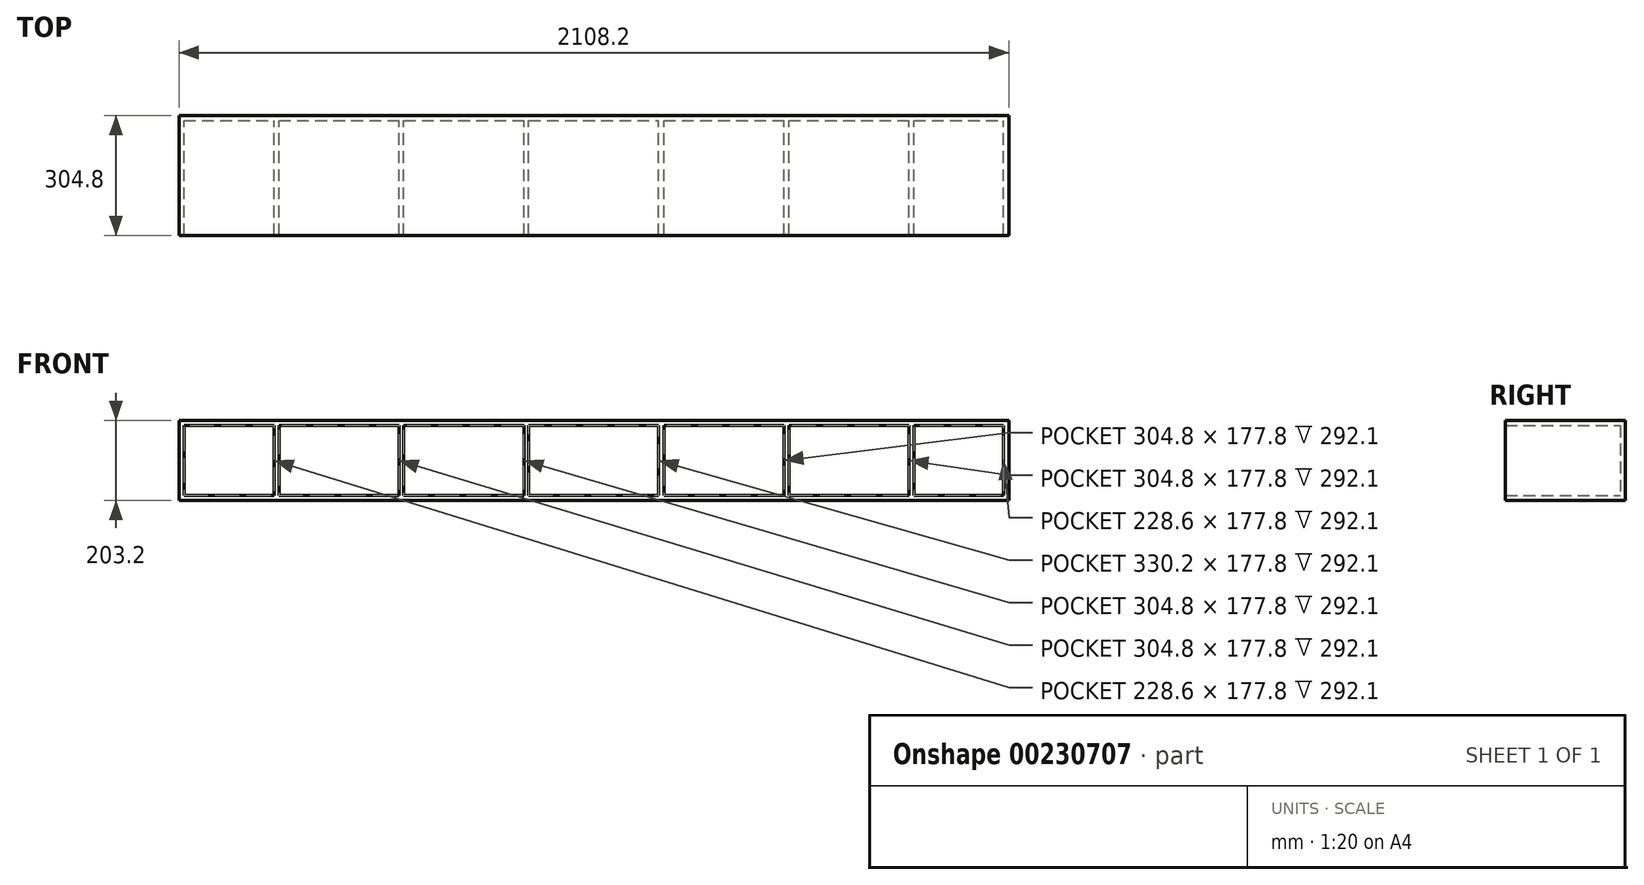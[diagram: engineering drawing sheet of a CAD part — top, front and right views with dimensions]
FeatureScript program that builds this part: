
annotation { "Feature Type Name" : "Feature", "Feature Type Description" : "" }
export const myFeature = defineFeature(function(context is Context, id is Id, definition is map)
    precondition{}
    {
        {
            var Q0;
            Q0=qCreatedBy(makeId("Front.planeOp"),FACE);
            var sketch = newSketch(context, id + "F0", { "sketchPlane" : qUnion([Q0])});
            skLineSegment(sketch, "E0.bottom", {"start": v(-1051.15, -136.83) * mm, "end": v(1057.05, -136.83) * mm});
            skLineSegment(sketch, "E0.top", {"start": v(-1051.15, -340.03) * mm, "end": v(1057.05, -340.03) * mm});
            skLineSegment(sketch, "E0.left", {"start": v(-1051.15, -136.83) * mm, "end": v(-1051.15, -340.03) * mm});
            skLineSegment(sketch, "E0.right", {"start": v(1057.05, -136.83) * mm, "end": v(1057.05, -340.03) * mm});
            skSolve(sketch);
        }
        {
            var Q0;
            Q0=makeQuery(id+"F0.imprint","IMPRINT",FACE,{"disambiguationData":[TD([[makeQuery(id+"F0.imprint","IMPRINT",EDGE,{"derivedFrom":sQuery(id+"F0.wireOp",EDGE,"E0.bottom")}),-1.0]])]});
            extrude(context, id + "F1", {"entities" : qUnion([Q0]), "depth" : 304.8 * mm});
        }
        {
            var Q0;
            Q0=makeQuery(id+"F1.opExtrude","CAP_FACE",FACE,{"disambiguationData":[OSD([sQuery(id+"F0.wireOp",EDGE,"E0.bottom"),sQuery(id+"F0.wireOp",EDGE,"E0.top"),sQuery(id+"F0.wireOp",EDGE,"E0.left"),sQuery(id+"F0.wireOp",EDGE,"E0.right")])],"isStart":false});
            shell(context, id + "F2", {"entities" : qUnion([Q0]), "thickness" : 12.7 * mm});
        }
        {
            var Q0;
            Q0=makeQuery(id+"F2.opShell","OFFSET_FACE",FACE,{"disambiguationData":[OSD([sQuery(id+"F0.wireOp",EDGE,"E0.bottom"),sQuery(id+"F0.wireOp",EDGE,"E0.top"),sQuery(id+"F0.wireOp",EDGE,"E0.left"),sQuery(id+"F0.wireOp",EDGE,"E0.right")])]});
            var sketch = newSketch(context, id + "F3", { "sketchPlane" : qUnion([Q0])});
            skLineSegment(sketch, "E1.bottom", {"start": v(-809.85, -149.53) * mm, "end": v(-797.15, -149.53) * mm});
            skLineSegment(sketch, "E1.top", {"start": v(-809.85, -327.33) * mm, "end": v(-797.15, -327.33) * mm});
            skLineSegment(sketch, "E1.left", {"start": v(-809.85, -149.53) * mm, "end": v(-809.85, -327.33) * mm});
            skLineSegment(sketch, "E1.right", {"start": v(-797.15, -149.53) * mm, "end": v(-797.15, -327.33) * mm});
            skLineSegment(sketch, "E2.bottom", {"start": v(-492.35, -149.53) * mm, "end": v(-479.65, -149.53) * mm});
            skLineSegment(sketch, "E2.top", {"start": v(-492.35, -327.33) * mm, "end": v(-479.65, -327.33) * mm});
            skLineSegment(sketch, "E2.left", {"start": v(-492.35, -149.53) * mm, "end": v(-492.35, -327.33) * mm});
            skLineSegment(sketch, "E2.right", {"start": v(-479.65, -149.53) * mm, "end": v(-479.65, -327.33) * mm});
            skLineSegment(sketch, "E3.bottom", {"start": v(-174.85, -149.53) * mm, "end": v(-162.15, -149.53) * mm});
            skLineSegment(sketch, "E3.top", {"start": v(-174.85, -327.33) * mm, "end": v(-162.15, -327.33) * mm});
            skLineSegment(sketch, "E3.left", {"start": v(-162.15, -149.53) * mm, "end": v(-162.15, -327.33) * mm});
            skLineSegment(sketch, "E3.right", {"start": v(-174.85, -149.53) * mm, "end": v(-174.85, -327.33) * mm});
            skLineSegment(sketch, "E4.bottom", {"start": v(815.75, -149.53) * mm, "end": v(803.05, -149.53) * mm});
            skLineSegment(sketch, "E4.top", {"start": v(815.75, -327.33) * mm, "end": v(803.05, -327.33) * mm});
            skLineSegment(sketch, "E4.left", {"start": v(815.75, -149.53) * mm, "end": v(815.75, -327.33) * mm});
            skLineSegment(sketch, "E4.right", {"start": v(803.05, -149.53) * mm, "end": v(803.05, -327.33) * mm});
            skLineSegment(sketch, "E5.bottom", {"start": v(498.25, -149.53) * mm, "end": v(485.55, -149.53) * mm});
            skLineSegment(sketch, "E5.top", {"start": v(498.25, -327.33) * mm, "end": v(485.55, -327.33) * mm});
            skLineSegment(sketch, "E5.left", {"start": v(498.25, -149.53) * mm, "end": v(498.25, -327.33) * mm});
            skLineSegment(sketch, "E5.right", {"start": v(485.55, -149.53) * mm, "end": v(485.55, -327.33) * mm});
            skLineSegment(sketch, "E6.bottom", {"start": v(180.75, -149.53) * mm, "end": v(168.05, -149.53) * mm});
            skLineSegment(sketch, "E6.top", {"start": v(180.75, -327.33) * mm, "end": v(168.05, -327.33) * mm});
            skLineSegment(sketch, "E6.left", {"start": v(180.75, -149.53) * mm, "end": v(180.75, -327.33) * mm});
            skLineSegment(sketch, "E6.right", {"start": v(168.05, -149.53) * mm, "end": v(168.05, -327.33) * mm});
            skSolve(sketch);
        }
        {
            var Q0;
            Q0=makeQuery(id+"F3.imprint","IMPRINT",FACE,{"disambiguationData":[TD([[makeQuery(id+"F3.imprint","IMPRINT",EDGE,{"derivedFrom":sQuery(id+"F3.wireOp",EDGE,"E1.bottom")}),-1.0]])]});
            var Q1;
            Q1=makeQuery(id+"F3.imprint","IMPRINT",FACE,{"disambiguationData":[TD([[makeQuery(id+"F3.imprint","IMPRINT",EDGE,{"derivedFrom":sQuery(id+"F3.wireOp",EDGE,"E2.bottom")}),-1.0]])]});
            var Q2;
            Q2=makeQuery(id+"F3.imprint","IMPRINT",FACE,{"disambiguationData":[TD([[makeQuery(id+"F3.imprint","IMPRINT",EDGE,{"derivedFrom":sQuery(id+"F3.wireOp",EDGE,"E3.bottom")}),-1.0]])]});
            var Q3;
            Q3=makeQuery(id+"F3.imprint","IMPRINT",FACE,{"disambiguationData":[TD([[makeQuery(id+"F3.imprint","IMPRINT",EDGE,{"derivedFrom":sQuery(id+"F3.wireOp",EDGE,"E6.bottom")}),-1.0]])]});
            var Q4;
            Q4=makeQuery(id+"F3.imprint","IMPRINT",FACE,{"disambiguationData":[TD([[makeQuery(id+"F3.imprint","IMPRINT",EDGE,{"derivedFrom":sQuery(id+"F3.wireOp",EDGE,"E5.bottom")}),-1.0]])]});
            var Q5;
            Q5=makeQuery(id+"F3.imprint","IMPRINT",FACE,{"disambiguationData":[TD([[makeQuery(id+"F3.imprint","IMPRINT",EDGE,{"derivedFrom":sQuery(id+"F3.wireOp",EDGE,"E4.bottom")}),-1.0]])]});
            extrude(context, id + "F4", {"entities" : qUnion([Q0, Q1, Q2, Q3, Q4, Q5]), "operationType" : NewBodyOperationType.ADD, "depth" : 292.1 * mm});
        }
    });
